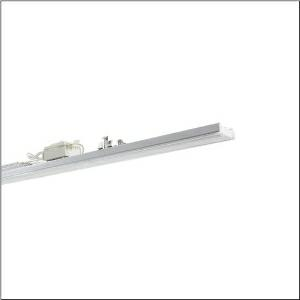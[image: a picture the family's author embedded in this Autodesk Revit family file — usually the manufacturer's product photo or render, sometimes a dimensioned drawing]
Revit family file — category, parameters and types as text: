
# Revit family: licross_r__21_recessed_ho_52tl1ecn4axs_dc99
name_source: partatom
category: Lighting Fixtures
units: mm (PartAtom-declared; Revit-internal decimal feet)

## family parameters
Cut with Voids When Loaded = No
Host = Face
Light Source = No
Part Type = Normal
Room Calculation Point = No
Round Connector Dimension = Use Diameter
Shared = No

## types (1)
- --- (1 x LED, 10030 lm, 54.7 W, 4000K)
    Apparent Load = 55 VA
    CIE Flux Codes = 85 95 99 100 100
    Color Rendering = 80
    Color Temperature = 4000K
    Default Elevation = 1800 mm
    Description = Licross® 21 Recessed HO, luminaire insert, of sheet steel, galvanised, coil coated, white, length: 1.500mm, width: 66mm, height: 67mm, LED rated luminous flux: 10.030lm, light colour: 840, control gear: ON/OFF Multilumen, CLOi, control gear: ECG Multilumen, with plug, 3-pole, with phase selection, mains connection: 220..240V, AC, 50/60Hz, start of lifetime: 55W, end of service life: 66W, halogen-free wiring, primary light control with lens, of plastic, primary optical cover: cover, of PMMA, light emission: direct distribution, primary light characteristic: symmetric, protection rating (complete): IP40, insulation class (complete): insulation class I (protective earthing), certification: CE, ENEC, VDE, UKCA, protection symbol: D if used in an environment without relevant dust loads with corresponding accessories, impact resistance: IK06, permissible ambient temperature for indoor applications: -35..+35°C, corresponds to IFS (International Featured Standards) requirements for safety and quality in the food industry, reducing of maximum allowable ambient temperature of 5°C with ceiling mounting, LABS conformity tested according to VDMA 24364:2018-05, packaging unit: 1 piece
    Height = 58 mm
    Lamp = 1 x LED
    Lamp Light Flux = 10030 lm
    Lamp Power = 54.7 W
    Lamp count = 1
    Length = 1500 mm
    Luminous efficacy = 183 lm/W
    Manufacturer = Siteco
    ModVariant = No
    Model = 52TL1ECN4AXS
    Mounting Place = Ceiling
    Mounting Type = Pendant
    Number of Poles = 1
    OnlyDefault = Yes
    Power Factor = 1
    Product Name = Licross® 21 Recessed HO
    Product group = luminaire insert
    ProductGroupID = 902
    Protection Class = Protection class I
    Protection Degree = IP 40
    RLX_Detail_Level = 1
    RLX_Emergency_Light_Flux = 0 lm
    RLX_Emergency_Type = 0
    RLX_Emergency_Type_DB = No
    RlxData = <blob elided: 22497 chars, md5=62e8d442>
    Socket = socket
    Standby Power = 0 W
    System Light Flux = 10030 lm
    System Power = 55 W
    Type Comments = factory setting: luminous flux: 100 % | (A | C | E) | 129 mA
    Type Image = l_1296930.jpg
    URL = http://relux.com
    VarID = @adj_109922
    Voltage = 0 V
    Weight = 0.00 kg
    Width = 66 mm

## geometry (parser evidence)
native form markers: Blend x4, Sweep x9
no freeform markers — native parametric forms only
